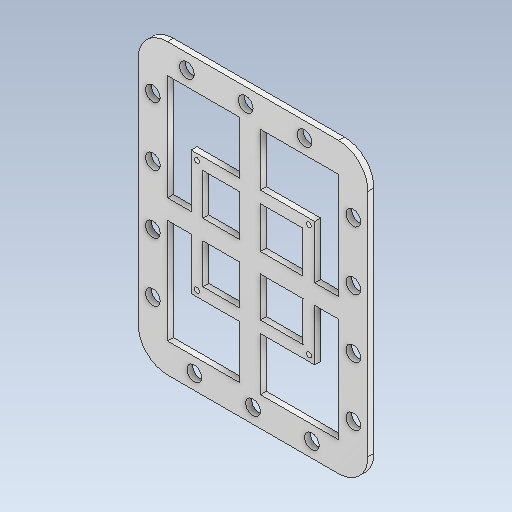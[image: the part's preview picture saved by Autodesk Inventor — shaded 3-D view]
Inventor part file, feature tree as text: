
AUTODESK INVENTOR PART (.ipt)
format: ipt  version: 2020 (Build 240168000, 168)  size: 247,808 bytes
history: native  units: in
note: dims shown in document units (in); Inventor stores cm internally (conversion verified against a paired STEP export)
features: other x6, reference x5, extrude x1, sketch x1
ambient origin geometry x8: Origin, YZ Plane, XZ Plane, XY Plane, X Axis, Y Axis, Z Axis, Center Point
bodies: Solid1 (feature_tree)
feature tree (13):
  extrude  "Extrusion1"  Depth=0.1in
  sketch  "Sketch1"  dims[d0=1.0in d1=1.0in d2=1.0in d3=1.0in d4=0.5in d5=0.5in d6=0.5in d7=0.5in d8=0.5in d9=0.5in d10=0.25in d11=0.4545in d12=1.1811in d14=1.0in d15=0.3937in d17=1.0in d21=0.25in d22=1.1811in d24=1.0in d25=0.3937in d27=1.0in d29=0.25in d30=1.5748in d32=1.0in d33=0.3937in d35=1.0in d37=0.25in d38=1.5748in d40=1.0in d41=0.3937in d43=1.0in d45=0.1in d46=0.0in]
  reference  "Reference1"
  reference  "Reference2"
  reference  "Reference3"
  reference  "Reference4"
  reference  "Reference5"
  other  "<userpath>\Documents\Inventor\Drone\Assembly.iam"
  other  "Assembly.iam"
  other  "standoff:4"
  other  "standoff:2"
  other  "standoff:3"
  other  "standoff:1"
